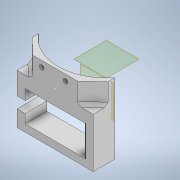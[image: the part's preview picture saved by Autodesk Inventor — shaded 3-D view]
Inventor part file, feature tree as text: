
AUTODESK INVENTOR PART (.ipt)
format: ipt  version: 2021 (Build 250183000, 183)  size: 209,920 bytes
history: native  units: mm
features: sketch x9, extrude x8, plane x2, other x1, chamfer x1
ambient origin geometry x8: Origin, YZ Plane, XZ Plane, XY Plane, X Axis, Y Axis, Z Axis, Center Point
bodies: Body1 (feature_tree)
feature tree (21):
  other  "Sólido1"
  plane  "Plano de trabajo1"
  extrude  "Extrusión2"  Depth=3.0mm
  plane  "Plano de trabajo2"
  extrude  "Extrusión3"  Depth=2.0mm
  extrude  "Extrusión4"  Depth=50.0mm
  extrude  "Extrusión5"  Depth=15.0mm
  extrude  "Extrusión6"  Depth=15.0mm TaperAngle=0.0deg
  extrude  "Extrusión7"  Depth=8.0mm
  extrude  "Extrusión8"  Depth=3.0mm
  extrude  "Extrusión9"  Depth=12.0mm TaperAngle=0.0deg
  sketch  "Boceto11"  dims[d36=8.0mm d37=0.0mm d38=20.5mm d39=20.5mm d40=20.2mm d41=20.2mm d43=7.0mm d44=6.0mm d45=14.5mm d46=0.0mm d47=5.0mm d48=0.0mm d49=10.0mm d50=14.0mm d51=0.0mm d52=2.0mm d53=2.0mm d54=45.0deg]
  chamfer  "Chaflán1"  Distance=2.0mm
  sketch  "Boceto2"  dims[d15=3.0mm d16=3.0mm]
  sketch  "Boceto4"  dims[d17=12.0mm d18=0.0mm d19=2.0mm]
  sketch  "Boceto5"  dims[d20=20.0mm d21=50.0mm]
  sketch  "Boceto6"  dims[d22=100.0mm d23=15.0mm]
  sketch  "Boceto7"  dims[d24=15.0mm d25=12.0mm d26=0.0mm]
  sketch  "Boceto8"  dims[d27=8.0mm d28=8.0mm]
  sketch  "Boceto9"  dims[d29=16.0mm d30=3.0mm]
  sketch  "Boceto10"  dims[d31=3.0mm d32=12.0mm d33=0.0mm d34=2.0mm d35=0.0mm]
